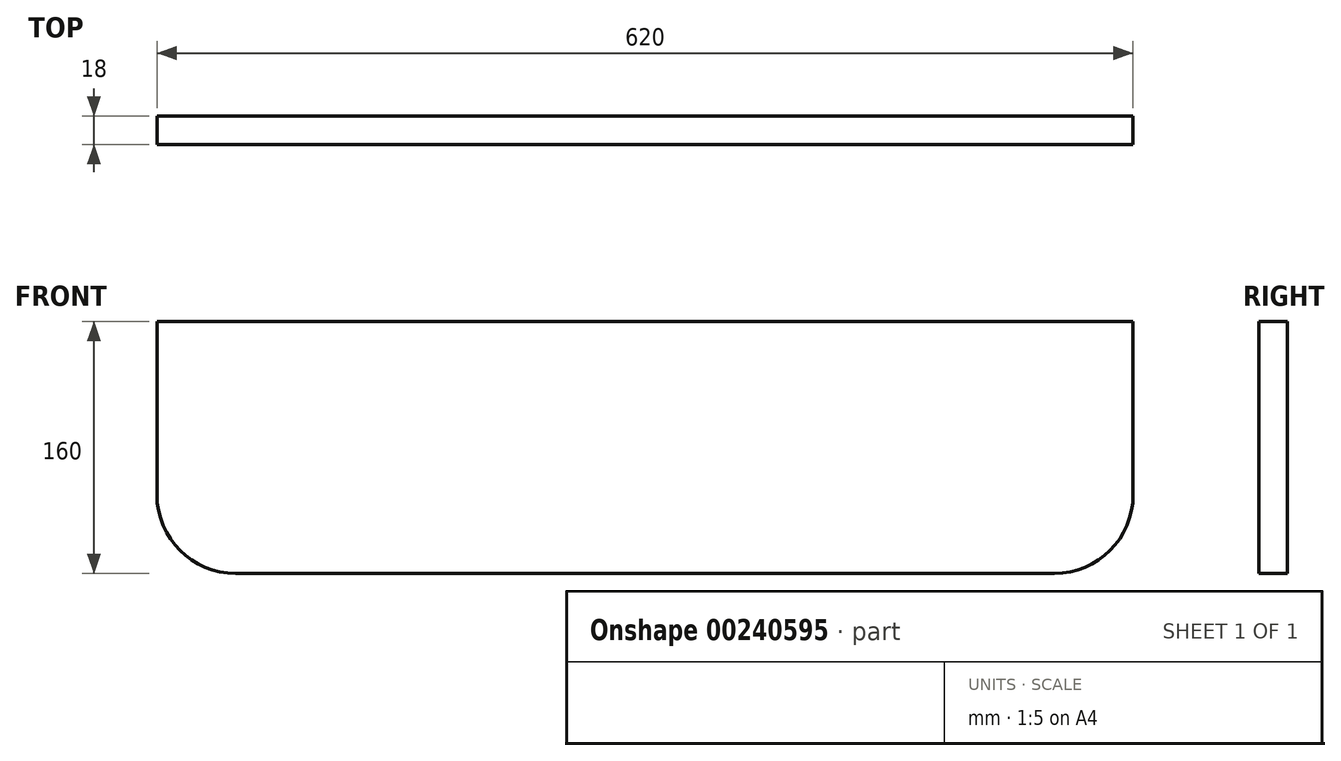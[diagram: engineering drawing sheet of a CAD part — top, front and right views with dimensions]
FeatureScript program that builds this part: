
annotation { "Feature Type Name" : "Feature", "Feature Type Description" : "" }
export const myFeature = defineFeature(function(context is Context, id is Id, definition is map)
    precondition{}
    {
        {
            var Q0;
            Q0=qCreatedBy(makeId("Front.planeOp"),FACE);
            var sketch = newSketch(context, id + "F0", { "sketchPlane" : qUnion([Q0])});
            skLineSegment(sketch, "E0.bottom", {"start": v(0, 0) * mm, "end": v(620, 0) * mm});
            skLineSegment(sketch, "E0.top", {"start": v(0, 160) * mm, "end": v(620, 160) * mm});
            skLineSegment(sketch, "E0.left", {"start": v(0, 0) * mm, "end": v(0, 160) * mm});
            skLineSegment(sketch, "E0.right", {"start": v(620, 0) * mm, "end": v(620, 160) * mm});
            skSolve(sketch);
        }
        {
            var Q0;
            Q0 = qSketchRegion(id + "F0", true);
            extrude(context, id + "F1", {"entities" : qUnion([Q0]), "depth" : 18 * mm, "offsetDistance" : 25 * mm});
        }
        {
            var Q0;
            Q0=makeQuery(id+"F1.opExtrude","SWEPT_EDGE",EDGE,{"disambiguationData":[OSD([sQuery(id+"F0.wireOp",EDGE,"E0.bottom"),sQuery(id+"F0.wireOp",EDGE,"E0.right")])]});
            var Q1;
            Q1=makeQuery(id+"F1.opExtrude","SWEPT_EDGE",EDGE,{"disambiguationData":[OSD([sQuery(id+"F0.wireOp",EDGE,"E0.bottom"),sQuery(id+"F0.wireOp",EDGE,"E0.left")])]});
            fillet(context, id + "F2", {"entities" : qUnion([Q0, Q1]), "radius" : 50 * mm, "tangentPropagation" : true, "allowEdgeOverflow" : false});
        }
    });
